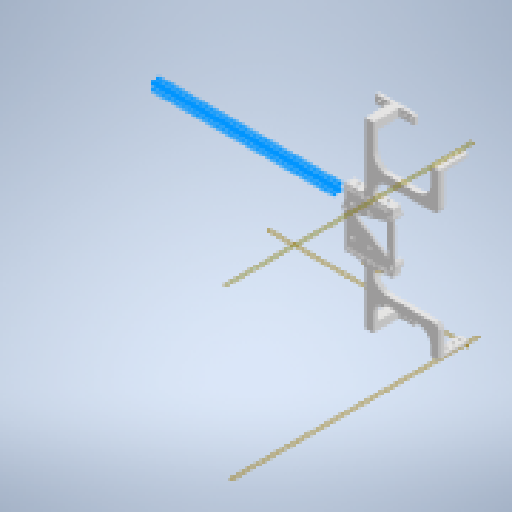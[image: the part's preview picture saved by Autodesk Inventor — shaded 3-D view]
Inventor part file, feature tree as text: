
AUTODESK INVENTOR PART (.ipt)
format: ipt  version: 2024.2 (Build 282272000, 272)  size: 1,190,912 bytes
history: native  units: mm
features: other x17, reference x16, sketch x11, extrude x11, thread x8, plane x6, projected_geometry x5, fillet x4
ambient origin geometry x8: Origin, YZ Plane, XZ Plane, XY Plane, X Axis, Y Axis, Z Axis, Center Point
bodies: Body1 (feature_tree)
feature tree (78):
  sketch  "Sketch1"  dims[d0=1.2mm d3=1.2mm]
  plane  "Work Plane1"
  extrude  "Extrusion4"  Depth=1.2mm
  extrude  "Extrusion5"  Depth=1.0mm
  extrude  "Extrusion6"  Depth=3.0mm TaperAngle=0.0deg
  fillet  "Fillet1"  Radius=7.5mm
  sketch  "Sketch7"  dims[d15=7.5mm d16=7.5mm]
  plane  "Work Plane2"
  extrude  "Extrusion7"  Depth=7.5mm
  extrude  "Extrusion8"  Depth=27.0mm
  extrude  "Extrusion9"  Depth=10.0mm
  thread  "Thread1"  [1 undecoded]
  thread  "Thread2"  [1 undecoded]
  thread  "Thread3"  [1 undecoded]
  thread  "Thread4"  [1 undecoded]
  thread  "Thread5"  [1 undecoded]
  thread  "Thread6"  [1 undecoded]
  thread  "Thread7"  [1 undecoded]
  thread  "Thread8"  [1 undecoded]
  extrude  "Extrusion10"  Depth=10.0mm
  fillet  "Fillet2"  Radius=10.0mm
  plane  "Work Plane3"
  extrude  "Extrusion11"  Depth=1.0mm TaperAngle=0.0deg
  plane  "Work Plane4"
  extrude  "Extrusion12"  Depth=1.0mm TaperAngle=0.0deg
  plane  "Work Plane5"
  extrude  "Extrusion13"  Depth=1.0mm TaperAngle=0.0deg
  sketch  "Sketch14"  dims[d47=1.0mm d48=0.0mm d49=1.0mm d50=0.0mm d51=1.0mm d52=0.0mm d55=10.0mm d56=45.0mm d57=35.0mm d59=10.0mm d61=10.0mm d62=10.0mm d63=6.0mm d64=0.0mm d65=6.25mm d66=3.2mm d67=5.0mm d68=30.0mm d70=7.5mm d71=10.0mm d73=10.0mm d75=4.0mm d76=0.0mm d77=4.0mm d78=0.0mm d79=3.2mm d80=3.2mm d81=5.0mm d82=7.5mm d83=5.0mm d84=4.0mm d85=0.0mm d86=4.0mm d87=0.0mm d88=15.75mm d89=6.25mm d1=0.5mm d2=0.872665mm d4=0.872665mm]
  plane  "Work Plane6"
  extrude  "Extrusion14"  Depth=6.25mm TaperAngle=0.0deg
  fillet  "Fillet3"  Radius=1.0mm
  fillet  "Fillet4"  Radius=10.0mm
  sketch  "Sketch5"  dims[d8=1.0mm d9=1.0mm]
  reference  "Reference9"
  reference  "Reference10"
  reference  "Reference11"
  reference  "Reference12"
  projected_geometry  "Projected Loop1"
  projected_geometry  "Projected Loop2"
  sketch  "Sketch6"  dims[d10=7.0mm d11=0.0mm d12=3.0mm d13=0.0mm d14=7.5mm]
  reference  "Reference13"
  reference  "Reference14"
  reference  "Reference15"
  projected_geometry  "Projected Loop3"
  projected_geometry  "Projected Loop4"
  sketch  "Sketch8"  dims[d17=3.0mm d18=0.0mm d19=27.0mm]
  sketch  "Sketch9"  dims[d20=7.0mm d21=7.0mm d22=7.0mm d23=3.0mm d24=0.0mm d25=3.5mm d26=3.5mm d27=3.5mm d28=3.5mm d29=10.0mm d30=0.0mm d31=3.2mm]
  sketch  "Sketch10"  dims[d32=10.0mm d33=3.2mm d34=10.0mm]
  reference  "Reference16"
  reference  "Reference17"
  reference  "Reference18"
  sketch  "Sketch11"  dims[d35=0.0mm d36=0.0mm d37=1.0mm d38=0.0mm]
  reference  "Reference19"
  reference  "Reference20"
  reference  "Reference22"
  sketch  "Sketch12"  dims[d39=1.0mm d40=0.0mm d41=1.0mm d42=0.0mm]
  projected_geometry  "Projected Loop5"
  sketch  "Sketch13"  dims[d43=1.0mm d44=0.0mm d45=1.0mm d46=0.0mm]
  reference  "Reference23"
  reference  "Reference24"
  reference  "Reference25"
  other  "<userpath>\Desktop\meca_robotbebou\iks01A2\iks01A2switch.iam"
  other  "iks01A2switch.iam"
  other  "zl262-20d_p2-54_l25-9_w5_h8-5:2"
  other  "zl262-20d_p2-54_l25-9_w5_h8-5:1"
  other  "zl262-20d_p2-54_l25-9_w5_h8-5:4"
  other  "zl262-20d_p2-54_l25-9_w5_h8-5:3"
  other  "NUCLEO-F411RE:1"
  other  "<userpath>\Desktop\meca_robotbebou\Robotbebou.iam"
  other  "Robotbebou.iam"
  other  "MakerBeam-cube_MIR:2"
  other  "MakerBeam-cube_MIR_MIR2:1"
  other  "profile210_MIR:1"
  other  "profile210:1"
  other  "profile190_MIR:1"
  other  "profile259:1"
  other  "profile259_MIR1:1"
  other  "profile210_MIR_MIR:1"
note: 8 required parameter values undecoded (feature->parameter linkage not recoverable at this tier; creation-order binding heuristic only, values carry confidence <= 0.55)
